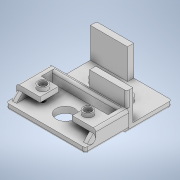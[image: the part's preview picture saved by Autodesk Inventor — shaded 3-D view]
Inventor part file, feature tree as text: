
AUTODESK INVENTOR PART (.ipt)
format: ipt  version: 2022 (Build 260153000, 153)  size: 307,200 bytes
history: native  units: in
note: dims shown in document units (in); Inventor stores cm internally (conversion verified against a paired STEP export)
features: extrude x11, sketch x11, chamfer x3, mirror x1, fillet x1
ambient origin geometry x8: Origin, YZ Plane, XZ Plane, XY Plane, X Axis, Y Axis, Z Axis, Center Point
bodies: Solid1 (feature_tree)
feature tree (27):
  extrude  "Extrusion1"  Depth=1.4331in
  extrude  "Extrusion2"  Depth=1.1811in
  extrude  "Extrusion3"  Depth=1.1811in
  extrude  "Extrusion4"  Depth=0.9606in TaperAngle=0.0deg
  extrude  "Extrusion5"  Depth=0.3406in
  chamfer  "Chamfer1"  Distance=0.1969in
  extrude  "Extrusion6"  Depth=0.1575in
  chamfer  "Chamfer2"  Distance=0.5906in
  extrude  "Extrusion7"  Depth=0.2362in
  extrude  "Extrusion8"  Depth=0.0787in TaperAngle=45.0deg
  mirror  "Mirror1"
  extrude  "Extrusion9"  Depth=0.1969in
  extrude  "Extrusion10"  Depth=0.0787in TaperAngle=45.0deg
  extrude  "Extrusion11"  Depth=0.0787in
  chamfer  "Chamfer3"  Distance=0.1969in
  fillet  "Fillet2"  Radius=0.1181in
  sketch  "Sketch1"  dims[d0=2.3937in d1=1.4331in]
  sketch  "Sketch2"  dims[d2=0.1969in d3=0.0in d4=1.1811in]
  sketch  "Sketch3"  dims[d5=0.1969in d6=1.1811in]
  sketch  "Sketch4"  dims[d7=0.1969in d8=0.9606in d9=0.0in]
  sketch  "Sketch5"  dims[d10=0.3406in d11=0.3406in d12=0.1969in d13=0.0in]
  sketch  "Sketch6"  dims[d14=0.1575in d15=0.1575in d16=0.5906in d17=0.0in]
  sketch  "Sketch7"  dims[d18=0.2362in d19=0.2362in]
  sketch  "Sketch8"  dims[d20=0.1181in d21=0.0in d22=0.0591in d23=0.0787in d24=45.0deg]
  sketch  "Sketch9"  dims[d26=2.5197in d27=0.1969in]
  sketch  "Sketch10"  dims[d28=1.378in d29=0.0in d30=0.1181in d31=0.0787in d32=45.0deg]
  sketch  "Sketch11"  dims[d33=0.1969in d34=1.0492in d35=0.1969in d36=0.1181in d37=0.3543in d38=0.0in d39=0.5906in d40=0.1575in d41=0.5512in d42=0.0in d43=0.315in d44=0.315in d45=0.1181in d46=0.0in d47=0.5906in d48=0.1575in d49=0.1575in d50=1.9685in d51=0.0in d52=0.2362in d53=0.2362in d54=0.1181in d55=0.0in d56=0.1969in d57=0.0787in d58=45.0deg d59=0.0787in]
